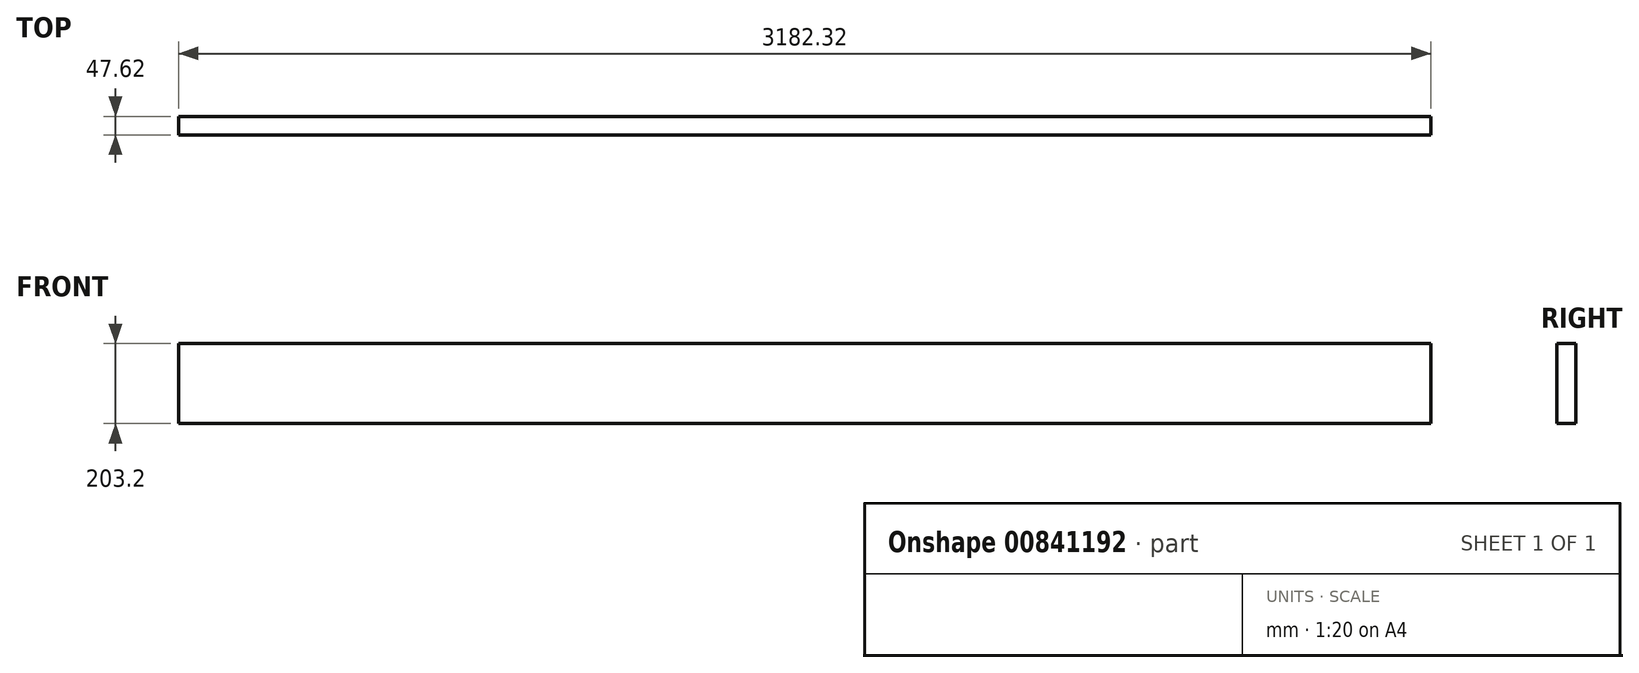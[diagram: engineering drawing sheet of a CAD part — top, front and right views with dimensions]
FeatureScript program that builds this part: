
annotation { "Feature Type Name" : "Feature", "Feature Type Description" : "" }
export const myFeature = defineFeature(function(context is Context, id is Id, definition is map)
    precondition{}
    {
        {
            var Q0;
            Q0=qCreatedBy(makeId("Right.planeOp"),FACE);
            var sketch = newSketch(context, id + "F0", { "sketchPlane" : qUnion([Q0])});
            skLineSegment(sketch, "E0.bottom", {"start": v(0, 0) * mm, "end": v(-47.63, 0) * mm});
            skLineSegment(sketch, "E0.top", {"start": v(0, -203.2) * mm, "end": v(-47.62, -203.2) * mm});
            skLineSegment(sketch, "E0.left", {"start": v(0, 0) * mm, "end": v(0, -203.2) * mm});
            skLineSegment(sketch, "E0.right", {"start": v(-47.63, 0) * mm, "end": v(-47.62, -203.2) * mm});
            skSolve(sketch);
        }
        {
            var Q0;
            Q0=makeQuery(id+"F0.imprint","IMPRINT",FACE,{"disambiguationData":[TD([[makeQuery(id+"F0.imprint","IMPRINT",EDGE,{"derivedFrom":sQuery(id+"F0.wireOp",EDGE,"E0.bottom")}),1.0]])]});
            extrude(context, id + "F1", {"entities" : qUnion([Q0]), "depth" : 3182.32 * mm, "offsetDistance" : 25.4 * mm});
        }
    });
